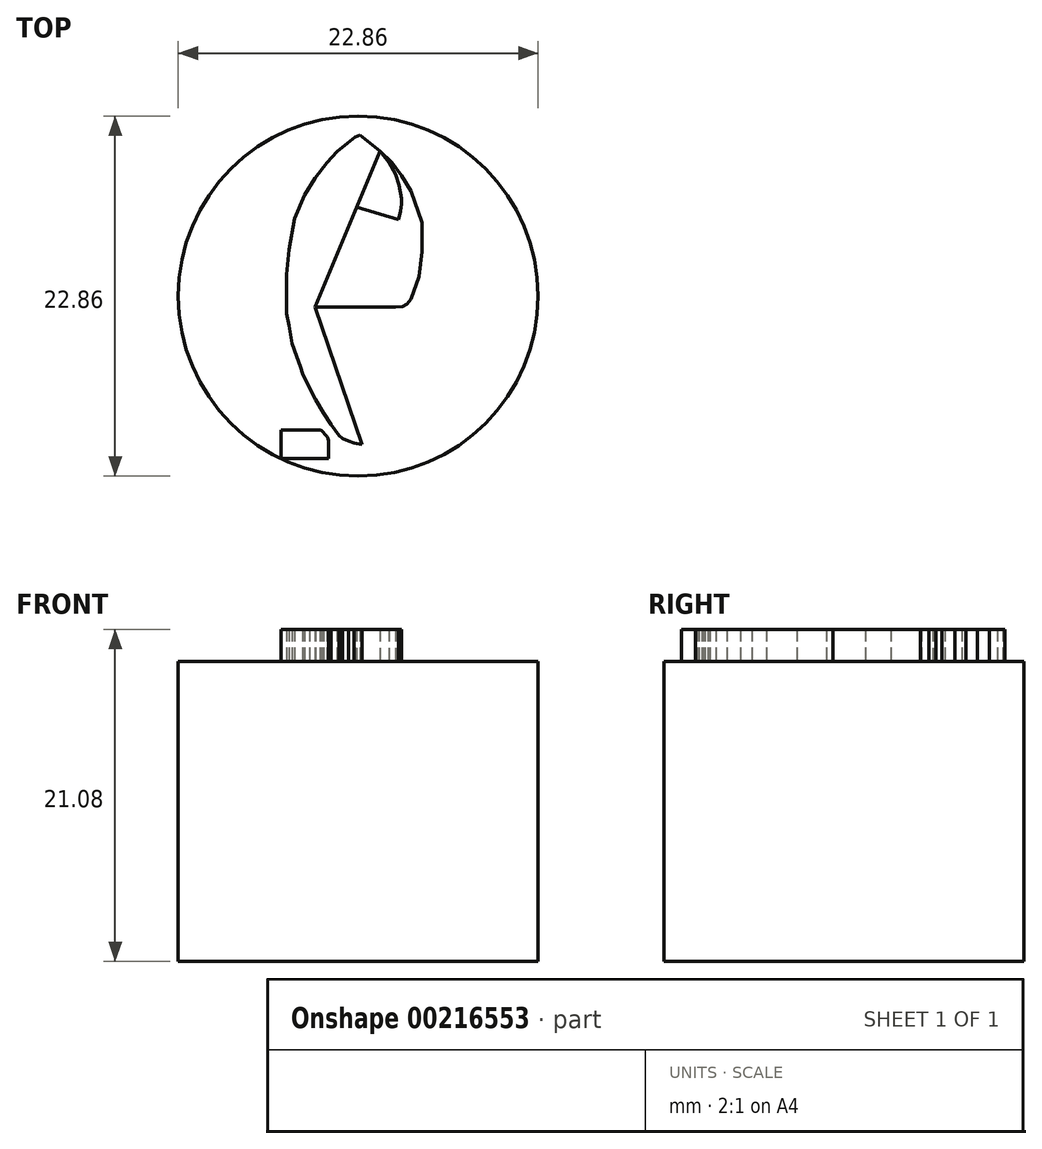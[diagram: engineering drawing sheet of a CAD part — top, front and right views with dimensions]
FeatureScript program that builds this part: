
annotation { "Feature Type Name" : "Feature", "Feature Type Description" : "" }
export const myFeature = defineFeature(function(context is Context, id is Id, definition is map)
    precondition{}
    {
        {
            var Q0;
            Q0=qCreatedBy(makeId("Top.planeOp"),FACE);
            var sketch = newSketch(context, id + "F0", { "sketchPlane" : qUnion([Q0])});
            skCircle(sketch, "E0", {"center": v(0, 0) * mm, "radius": 11.43 * mm});
            skSolve(sketch);
        }
        {
            var Q0;
            Q0=qSketchRegion(id+"F0",true);
            extrude(context, id + "F1", {"entities" : qUnion([Q0]), "depth" : 19.05 * mm});
        }
        {
            var Q0;
            Q0=makeQuery(id+"F1.opExtrude","CAP_FACE",FACE,{"disambiguationData":[OSD([sQuery(id+"F0.wireOp",EDGE,"E0")])],"isStart":false});
            var sketch = newSketch(context, id + "F2", { "sketchPlane" : qUnion([Q0])});
            skLineSegment(sketch, "E1", {"start": v(-1.88, -9.2) * mm, "end": v(-1.88, -9.88) * mm});
            skLineSegment(sketch, "E2", {"start": v(-1.88, -9.88) * mm, "end": v(-1.88, -10.33) * mm});
            skLineSegment(sketch, "E3", {"start": v(-4.89, -10.33) * mm, "end": v(-4.89, -8.51) * mm});
            skLineSegment(sketch, "E4", {"start": v(-4.89, -10.33) * mm, "end": v(-1.88, -10.33) * mm});
            skLineSegment(sketch, "E5", {"start": v(-1.88, -9.2) * mm, "end": v(-1.92, -9.03) * mm});
            skLineSegment(sketch, "E6", {"start": v(-1.92, -9.03) * mm, "end": v(-1.98, -8.92) * mm});
            skLineSegment(sketch, "E7", {"start": v(-1.98, -8.92) * mm, "end": v(-2.1, -8.78) * mm});
            skLineSegment(sketch, "E8", {"start": v(-2.1, -8.78) * mm, "end": v(-2.24, -8.63) * mm});
            skLineSegment(sketch, "E9", {"start": v(-2.24, -8.63) * mm, "end": v(-2.34, -8.55) * mm});
            skLineSegment(sketch, "E10", {"start": v(-2.34, -8.55) * mm, "end": v(-2.4, -8.51) * mm});
            skLineSegment(sketch, "E11", {"start": v(-4.89, -8.51) * mm, "end": v(-2.4, -8.51) * mm});
            skSolve(sketch);
        }
        {
            var Q0;
            Q0=makeQuery(id+"F1.opExtrude","CAP_FACE",FACE,{"disambiguationData":[OSD([sQuery(id+"F0.wireOp",EDGE,"E0")])],"isStart":false});
            var sketch = newSketch(context, id + "F3", { "sketchPlane" : qUnion([Q0])});
            skLineSegment(sketch, "E12", {"start": v(-1.22, -8.85) * mm, "end": v(-1.73, -8.15) * mm});
            skLineSegment(sketch, "E13", {"start": v(-1.73, -8.15) * mm, "end": v(-2.18, -7.42) * mm});
            skLineSegment(sketch, "E14", {"start": v(-2.18, -7.42) * mm, "end": v(-2.7, -6.58) * mm});
            skLineSegment(sketch, "E15", {"start": v(-2.7, -6.58) * mm, "end": v(-3.1, -5.86) * mm});
            skLineSegment(sketch, "E16", {"start": v(-3.1, -5.86) * mm, "end": v(-3.52, -4.93) * mm});
            skLineSegment(sketch, "E17", {"start": v(-3.52, -4.93) * mm, "end": v(-3.66, -4.52) * mm});
            skLineSegment(sketch, "E18", {"start": v(-3.66, -4.52) * mm, "end": v(-3.9, -3.8) * mm});
            skLineSegment(sketch, "E19", {"start": v(-3.9, -3.8) * mm, "end": v(-4.18, -3) * mm});
            skLineSegment(sketch, "E20", {"start": v(-4.18, -3) * mm, "end": v(-4.4, -1.87) * mm});
            skLineSegment(sketch, "E21", {"start": v(-4.4, -1.87) * mm, "end": v(-4.56, -1.1) * mm});
            skLineSegment(sketch, "E22", {"start": v(-4.56, -1.1) * mm, "end": v(-4.56, -0.45) * mm});
            skLineSegment(sketch, "E23", {"start": v(-4.56, -0.45) * mm, "end": v(-4.56, 0.53) * mm});
            skPoint(sketch, "E23.endSnap0", {"position": v(-4.56, -0.78) * mm});
            skLineSegment(sketch, "E24", {"start": v(-4.56, 0.53) * mm, "end": v(-4.56, 1.37) * mm});
            skLineSegment(sketch, "E25", {"start": v(-4.56, 1.37) * mm, "end": v(-4.4, 2.97) * mm});
            skLineSegment(sketch, "E26", {"start": v(-4.4, 2.97) * mm, "end": v(-4.2, 4) * mm});
            skLineSegment(sketch, "E27", {"start": v(-4.2, 4) * mm, "end": v(-4.02, 4.92) * mm});
            skLineSegment(sketch, "E28", {"start": v(-4.02, 4.92) * mm, "end": v(-3.4, 6.41) * mm});
            skLineSegment(sketch, "E29", {"start": v(-3.4, 6.41) * mm, "end": v(-2.75, 7.5) * mm});
            skLineSegment(sketch, "E30", {"start": v(-2.75, 7.5) * mm, "end": v(-1.98, 8.47) * mm});
            skLineSegment(sketch, "E31", {"start": v(-1.98, 8.47) * mm, "end": v(-1.34, 9.17) * mm});
            skLineSegment(sketch, "E32", {"start": v(-1.34, 9.17) * mm, "end": v(-0.69, 9.73) * mm});
            skLineSegment(sketch, "E33", {"start": v(-0.69, 9.73) * mm, "end": v(-0.2, 10.1) * mm});
            skLineSegment(sketch, "E34", {"start": v(-0.2, 10.1) * mm, "end": v(0.13, 10.21) * mm});
            skLineSegment(sketch, "E35", {"start": v(0.13, 10.21) * mm, "end": v(0.47, 9.94) * mm});
            skLineSegment(sketch, "E36", {"start": v(0.47, 9.94) * mm, "end": v(1.39, 9.22) * mm});
            skLineSegment(sketch, "E37", {"start": v(1.39, 9.22) * mm, "end": v(2.14, 8.47) * mm});
            skLineSegment(sketch, "E38", {"start": v(2.14, 8.47) * mm, "end": v(2.75, 7.65) * mm});
            skLineSegment(sketch, "E39", {"start": v(2.75, 7.65) * mm, "end": v(3.35, 6.68) * mm});
            skLineSegment(sketch, "E40", {"start": v(3.35, 6.68) * mm, "end": v(3.7, 5.67) * mm});
            skLineSegment(sketch, "E41", {"start": v(3.7, 5.67) * mm, "end": v(4.05, 4.66) * mm});
            skLineSegment(sketch, "E42", {"start": v(4.05, 4.66) * mm, "end": v(4.05, 3.83) * mm});
            skLineSegment(sketch, "E43", {"start": v(4.05, 3.83) * mm, "end": v(4.05, 2.82) * mm});
            skLineSegment(sketch, "E44", {"start": v(4.05, 2.82) * mm, "end": v(3.85, 1.23) * mm});
            skLineSegment(sketch, "E45", {"start": v(3.85, 1.23) * mm, "end": v(3.35, -0.18) * mm});
            skLineSegment(sketch, "E46", {"start": v(3.35, -0.18) * mm, "end": v(3.09, -0.52) * mm});
            skLineSegment(sketch, "E47", {"start": v(3.09, -0.52) * mm, "end": v(2.83, -0.66) * mm});
            skLineSegment(sketch, "E48", {"start": v(2.83, -0.66) * mm, "end": v(2.38, -0.7) * mm});
            skLineSegment(sketch, "E49", {"start": v(2.38, -0.7) * mm, "end": v(-2.75, -0.7) * mm});
            skLineSegment(sketch, "E50", {"start": v(-2.75, -0.7) * mm, "end": v(0.26, -9.43) * mm});
            skLineSegment(sketch, "E51", {"start": v(0.26, -9.43) * mm, "end": v(-0.26, -9.33) * mm});
            skLineSegment(sketch, "E52", {"start": v(-0.26, -9.33) * mm, "end": v(-0.62, -9.21) * mm});
            skLineSegment(sketch, "E53", {"start": v(-0.62, -9.21) * mm, "end": v(-1, -9.03) * mm});
            skLineSegment(sketch, "E54", {"start": v(-1, -9.03) * mm, "end": v(-1.22, -8.85) * mm});
            skSolve(sketch);
        }
        {
            var Q0;
            Q0=qSketchRegion(id+"F2",true);
            extrude(context, id + "F4", {"entities" : qUnion([Q0]), "operationType" : NewBodyOperationType.ADD, "depth" : 2.03 * mm});
        }
        {
            var Q0;
            Q0=qSketchRegion(id+"F3",true);
            extrude(context, id + "F5", {"entities" : qUnion([Q0]), "operationType" : NewBodyOperationType.ADD, "depth" : 2.03 * mm});
        }
        {
            var Q0;
            Q0=makeQuery(id+"F5.opExtrude","CAP_FACE",FACE,{"disambiguationData":[OSD([sQuery(id+"F3.wireOp",EDGE,"E12"),sQuery(id+"F3.wireOp",EDGE,"E13"),sQuery(id+"F3.wireOp",EDGE,"E14"),sQuery(id+"F3.wireOp",EDGE,"E15"),sQuery(id+"F3.wireOp",EDGE,"E16"),sQuery(id+"F3.wireOp",EDGE,"E17"),sQuery(id+"F3.wireOp",EDGE,"E18"),sQuery(id+"F3.wireOp",EDGE,"E19"),sQuery(id+"F3.wireOp",EDGE,"E20"),sQuery(id+"F3.wireOp",EDGE,"E21"),sQuery(id+"F3.wireOp",EDGE,"E22"),sQuery(id+"F3.wireOp",EDGE,"E23"),sQuery(id+"F3.wireOp",EDGE,"E24"),sQuery(id+"F3.wireOp",EDGE,"E25"),sQuery(id+"F3.wireOp",EDGE,"E26"),sQuery(id+"F3.wireOp",EDGE,"E27"),sQuery(id+"F3.wireOp",EDGE,"E28"),sQuery(id+"F3.wireOp",EDGE,"E29"),sQuery(id+"F3.wireOp",EDGE,"E30"),sQuery(id+"F3.wireOp",EDGE,"E31"),sQuery(id+"F3.wireOp",EDGE,"E32"),sQuery(id+"F3.wireOp",EDGE,"E33"),sQuery(id+"F3.wireOp",EDGE,"E34"),sQuery(id+"F3.wireOp",EDGE,"E35"),sQuery(id+"F3.wireOp",EDGE,"E36"),sQuery(id+"F3.wireOp",EDGE,"E37"),sQuery(id+"F3.wireOp",EDGE,"E38"),sQuery(id+"F3.wireOp",EDGE,"E39"),sQuery(id+"F3.wireOp",EDGE,"E40"),sQuery(id+"F3.wireOp",EDGE,"E41"),sQuery(id+"F3.wireOp",EDGE,"E42"),sQuery(id+"F3.wireOp",EDGE,"E43"),sQuery(id+"F3.wireOp",EDGE,"E44"),sQuery(id+"F3.wireOp",EDGE,"E45"),sQuery(id+"F3.wireOp",EDGE,"E46"),sQuery(id+"F3.wireOp",EDGE,"E47"),sQuery(id+"F3.wireOp",EDGE,"E48"),sQuery(id+"F3.wireOp",EDGE,"E49"),sQuery(id+"F3.wireOp",EDGE,"E50"),sQuery(id+"F3.wireOp",EDGE,"E51"),sQuery(id+"F3.wireOp",EDGE,"E52"),sQuery(id+"F3.wireOp",EDGE,"E53"),sQuery(id+"F3.wireOp",EDGE,"E54")])],"isStart":false});
            var sketch = newSketch(context, id + "F6", { "sketchPlane" : qUnion([Q0])});
            skLineSegment(sketch, "E55", {"start": v(-2.75, -0.7) * mm, "end": v(1.39, 9.22) * mm});
            skLineSegment(sketch, "E56", {"start": v(1.39, 9.22) * mm, "end": v(2.14, 8.47) * mm});
            skLineSegment(sketch, "E57", {"start": v(2.14, 8.47) * mm, "end": v(2.75, 7.65) * mm});
            skLineSegment(sketch, "E58", {"start": v(2.75, 7.65) * mm, "end": v(3.35, 6.68) * mm});
            skLineSegment(sketch, "E59", {"start": v(3.35, 6.68) * mm, "end": v(4.05, 4.66) * mm});
            skLineSegment(sketch, "E60", {"start": v(4.05, 4.66) * mm, "end": v(4.05, 2.82) * mm});
            skLineSegment(sketch, "E61", {"start": v(4.05, 2.82) * mm, "end": v(3.85, 1.23) * mm});
            skLineSegment(sketch, "E62", {"start": v(3.85, 1.23) * mm, "end": v(3.35, -0.18) * mm});
            skLineSegment(sketch, "E63", {"start": v(3.35, -0.18) * mm, "end": v(3.09, -0.52) * mm});
            skLineSegment(sketch, "E64", {"start": v(3.09, -0.52) * mm, "end": v(2.83, -0.66) * mm});
            skLineSegment(sketch, "E65", {"start": v(2.83, -0.66) * mm, "end": v(2.38, -0.7) * mm});
            skLineSegment(sketch, "E66", {"start": v(2.38, -0.7) * mm, "end": v(-2.75, -0.7) * mm});
            skSolve(sketch);
        }
        {
            var Q0;
            Q0 = qSketchRegion(id + "F6", true);
            extrude(context, id + "F7", {"entities" : qUnion([Q0]), "operationType" : NewBodyOperationType.REMOVE, "oppositeDirection" : true, "depth" : 2.04 * mm});
        }
        {
            var Q0;
            Q0=makeQuery(id+"F7.boolean.opBoolean","COPY",FACE,{"derivedFrom":makeQuery(id+"F7.opExtrude","CAP_FACE",FACE,{"disambiguationData":[OSD([sQuery(id+"F6.wireOp",EDGE,"E55"),sQuery(id+"F6.wireOp",EDGE,"E56"),sQuery(id+"F6.wireOp",EDGE,"E57"),sQuery(id+"F6.wireOp",EDGE,"E58"),sQuery(id+"F6.wireOp",EDGE,"E59"),sQuery(id+"F6.wireOp",EDGE,"E60"),sQuery(id+"F6.wireOp",EDGE,"E61"),sQuery(id+"F6.wireOp",EDGE,"E62"),sQuery(id+"F6.wireOp",EDGE,"E63"),sQuery(id+"F6.wireOp",EDGE,"E64"),sQuery(id+"F6.wireOp",EDGE,"E65"),sQuery(id+"F6.wireOp",EDGE,"E66")])],"isStart":false})});
            var sketch = newSketch(context, id + "F8", { "sketchPlane" : qUnion([Q0])});
            skLineSegment(sketch, "E67", {"start": v(1.39, 9.22) * mm, "end": v(1.95, 8.47) * mm});
            skLineSegment(sketch, "E68", {"start": v(1.95, 8.47) * mm, "end": v(2.37, 7.75) * mm});
            skLineSegment(sketch, "E69", {"start": v(2.37, 7.75) * mm, "end": v(2.6, 7.06) * mm});
            skLineSegment(sketch, "E70", {"start": v(2.6, 7.06) * mm, "end": v(2.75, 6.2) * mm});
            skLineSegment(sketch, "E71", {"start": v(2.75, 6.2) * mm, "end": v(2.75, 5.83) * mm});
            skLineSegment(sketch, "E72", {"start": v(2.75, 5.83) * mm, "end": v(2.68, 5.4) * mm});
            skLineSegment(sketch, "E73", {"start": v(2.68, 5.4) * mm, "end": v(2.56, 4.84) * mm});
            skLineSegment(sketch, "E74", {"start": v(2.56, 4.84) * mm, "end": v(-0.1, 5.66) * mm});
            skLineSegment(sketch, "E75", {"start": v(-0.1, 5.66) * mm, "end": v(1.39, 9.22) * mm});
            skSolve(sketch);
        }
        {
            var Q0;
            Q0 = qSketchRegion(id + "F8", true);
            extrude(context, id + "F9", {"entities" : qUnion([Q0]), "operationType" : NewBodyOperationType.ADD, "depth" : 2.03 * mm});
        }
        {
            var Q0;
            Q0=makeQuery(id+"F1.opExtrude","CAP_FACE",FACE,{"disambiguationData":[OSD([sQuery(id+"F0.wireOp",EDGE,"E0")])],"isStart":false});
            var sketch = newSketch(context, id + "F10", { "sketchPlane" : qUnion([Q0])});
            skCircle(sketch, "E76", {"center": v(3.37, 2.67) * mm, "radius": 0.76 * mm});
            skSolve(sketch);
        }
        {
            var Q0;
            Q0=sQuery(id+"F10.wireOp",EDGE,"E76");
            extrude(context, id + "F11", {"bodyType" : ToolBodyType.SURFACE, "surfaceEntities" : qUnion([Q0]), "depth" : 6.35 * mm});
        }
    });
